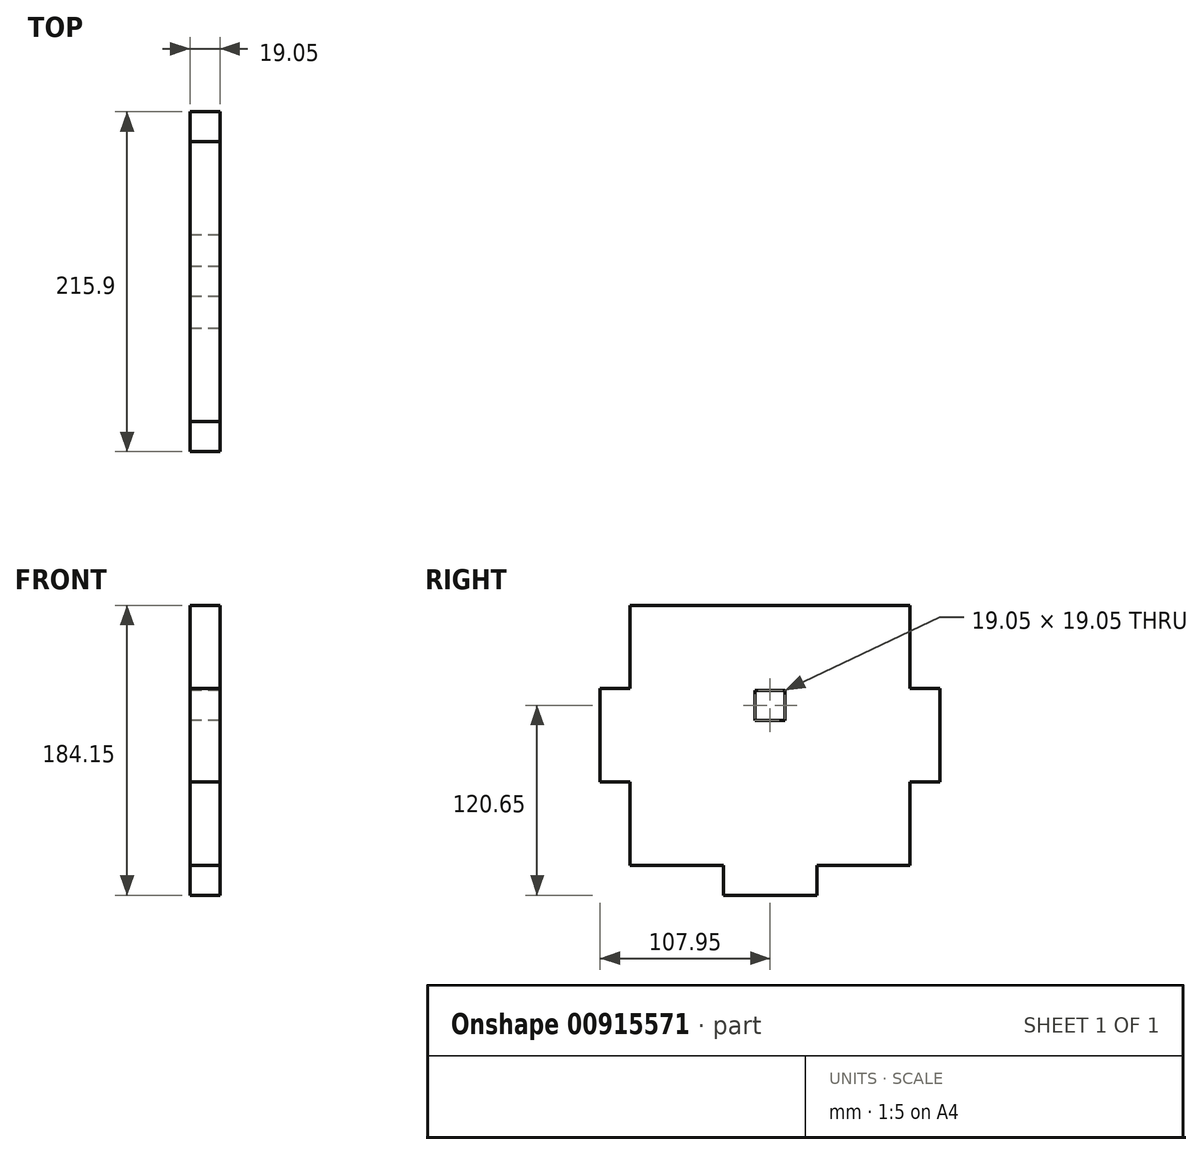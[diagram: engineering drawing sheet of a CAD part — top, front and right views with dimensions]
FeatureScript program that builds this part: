
annotation { "Feature Type Name" : "Feature", "Feature Type Description" : "" }
export const myFeature = defineFeature(function(context is Context, id is Id, definition is map)
    precondition{}
    {
        {
            var Q0;
            Q0=qCreatedBy(makeId("Right.planeOp"),FACE);
            var sketch = newSketch(context, id + "F0", { "sketchPlane" : qUnion([Q0])});
            skLineSegment(sketch, "E0.bottom", {"start": v(-88.9, 82.55) * mm, "end": v(88.9, 82.55) * mm});
            skPoint(sketch, "E0.middle", {"position": v(0, 0) * mm});
            skLineSegment(sketch, "E1", {"start": v(0, -101.6) * mm, "end": v(29.63, -101.6) * mm});
            skLineSegment(sketch, "E2", {"start": v(0, -101.6) * mm, "end": v(-29.63, -101.6) * mm});
            skLineSegment(sketch, "E3", {"start": v(-29.63, -101.6) * mm, "end": v(-29.63, -82.55) * mm});
            skLineSegment(sketch, "E4.top", {"start": v(-29.63, -101.6) * mm, "end": v(29.63, -101.6) * mm});
            skLineSegment(sketch, "E4.left", {"start": v(-29.63, -82.55) * mm, "end": v(-29.63, -101.6) * mm});
            skLineSegment(sketch, "E4.right", {"start": v(29.63, -82.55) * mm, "end": v(29.63, -101.6) * mm});
            skLineSegment(sketch, "E5", {"start": v(88.9, -82.55) * mm, "end": v(29.63, -82.55) * mm});
            skLineSegment(sketch, "E6", {"start": v(-29.63, -82.55) * mm, "end": v(-88.9, -82.55) * mm});
            skLineSegment(sketch, "E7.bottom", {"start": v(-9.53, 28.57) * mm, "end": v(9.53, 28.57) * mm});
            skLineSegment(sketch, "E7.top", {"start": v(-9.53, 9.52) * mm, "end": v(9.52, 9.52) * mm});
            skLineSegment(sketch, "E7.left", {"start": v(-9.53, 28.57) * mm, "end": v(-9.53, 9.52) * mm});
            skLineSegment(sketch, "E7.right", {"start": v(9.53, 28.57) * mm, "end": v(9.52, 9.52) * mm});
            skPoint(sketch, "E7.middle", {"position": v(0, 19.05) * mm});
            skLineSegment(sketch, "E8", {"start": v(-107.95, 0) * mm, "end": v(-107.95, 29.63) * mm});
            skLineSegment(sketch, "E9", {"start": v(-107.95, 0) * mm, "end": v(-107.95, -29.63) * mm});
            skLineSegment(sketch, "E10", {"start": v(-107.95, -29.63) * mm, "end": v(-88.9, -29.63) * mm});
            skLineSegment(sketch, "E11.bottom", {"start": v(-88.9, -29.63) * mm, "end": v(-107.95, -29.63) * mm});
            skLineSegment(sketch, "E11.top", {"start": v(-88.9, 29.63) * mm, "end": v(-107.95, 29.63) * mm});
            skLineSegment(sketch, "E11.right", {"start": v(-107.95, -29.63) * mm, "end": v(-107.95, 29.63) * mm});
            skLineSegment(sketch, "E12", {"start": v(-88.9, 29.63) * mm, "end": v(-88.9, 82.55) * mm});
            skLineSegment(sketch, "E13", {"start": v(-88.9, -29.63) * mm, "end": v(-88.9, -82.55) * mm});
            skLineSegment(sketch, "E14", {"start": v(107.95, 0) * mm, "end": v(107.95, 29.63) * mm});
            skLineSegment(sketch, "E15", {"start": v(107.95, 0) * mm, "end": v(107.95, -29.63) * mm});
            skLineSegment(sketch, "E16", {"start": v(107.95, -29.63) * mm, "end": v(88.9, -29.63) * mm});
            skLineSegment(sketch, "E17.bottom", {"start": v(88.9, -29.63) * mm, "end": v(107.95, -29.63) * mm});
            skLineSegment(sketch, "E17.top", {"start": v(88.9, 29.63) * mm, "end": v(107.95, 29.63) * mm});
            skLineSegment(sketch, "E17.right", {"start": v(107.95, -29.63) * mm, "end": v(107.95, 29.63) * mm});
            skLineSegment(sketch, "E18", {"start": v(88.9, -82.55) * mm, "end": v(88.9, -29.63) * mm});
            skLineSegment(sketch, "E19", {"start": v(88.9, 29.63) * mm, "end": v(88.9, 82.55) * mm});
            skSolve(sketch);
        }
        {
            var Q0;
            Q0=makeQuery(id+"F0.imprint","IMPRINT",FACE,{"disambiguationData":[TD([[makeQuery(id+"F0.imprint","IMPRINT",EDGE,{"derivedFrom":sQuery(id+"F0.wireOp",EDGE,"E0.bottom")}),-1.0]])]});
            extrude(context, id + "F1", {"entities" : qUnion([Q0]), "depth" : 19.05 * mm, "offsetDistance" : 25.4 * mm});
        }
    });
